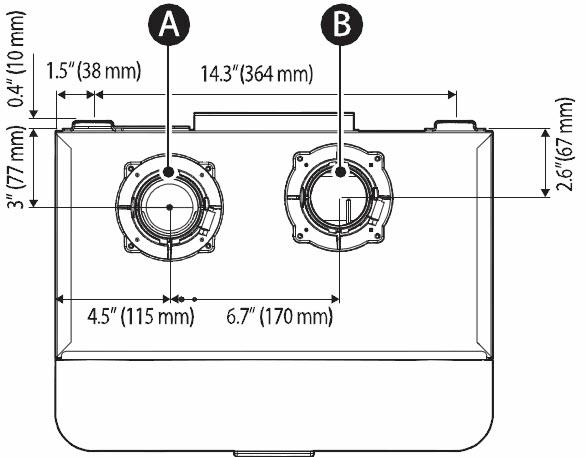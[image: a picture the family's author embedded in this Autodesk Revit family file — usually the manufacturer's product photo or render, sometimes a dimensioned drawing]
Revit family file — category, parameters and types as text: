
# Revit family: Water_Heater-Racks-Navien-NPE-12_Unit_Back_to_Back---
name_source: partatom
category: Mechanical Equipment
revit_build: Autodesk Revit 2016 (Build: 20150220_1215(x64)
units: mm (PartAtom-declared; Revit-internal decimal feet)

## family parameters
Cut with Voids When Loaded = No
Host = Face
OmniClass Number = 23.65.35.11
OmniClass Title = Supply Water Heaters
Part Type = Normal
Room Calculation Point = No
Round Connector Dimension = Use Diameter
Shared = No

## types (4) — shared parameters
2" Exhaust/Intake = Yes
3" Exhaust/Intake = No
Apparent Load = 0 VA
Assembly Code = D3010500
Certifications = Energy Star | AHRI | CSA | CSA | NFS
Cold Water Inlet = 1"
Configuration = NPE_B12_4B2B_4B2B
Default Elevation = 48 "
Depth = 23.8 "
Description = 12 Unit Back to Back
Exhaust = 2"
Finish = Metal - Navien - White
Flow Rate = 1 GPM
Flow Rate Note = 35°F (19°C) temp rise: 11.2 GPM (42 L/m) | 45°F (25°C) temp rise: 8.7 GPM (33 L/m) | 67°F (36°C) temp rise: NPE-240A: 5.6 GPM(21 L/m), NPE-240S: 5.7 GPM(22 L/m)
Frequency = 60 Hz
Gas Inlet = 1"
Heating Capacity = 120000.0 Btu/h
Heating Capacity Note = 19,900–199,900 (BTU/H)
Height = 65.5 "
Hot Water Outlet = 1"
Ignition = Electronic ignition
Installation Type = Indoor
Intake = 2"
Keynote = 22 33 00.A1
Manifold(s) = (2) 30019039A + (2) 30019042A
Manufacturer = Navien, Inc.
Manufacturer Fax Number = (949) 420-0430
Natural Gas Manifold Pressure = -0.05" WC to -0.58" WC
Natural Gas Supply Pressure = 3.5"–10.5" WC
Number of Poles = 1
Phase = 1
Power Factor = 1
Product Documentation Link = https://www.navieninc.com
Product Name = NPE Series Tankless Water Heaters w/ Racks
Product Page URL = https://www.navieninc.com
Propane Gas Manifold Pressure = -0.10" WC to -0.78" WC
Propane Gas Supply Pressure = 8"–13" WC
Rack(s) = (2) GFFM-KDIZUS-003 + (4) GFFM-KDIZUS-004
Required Cascade Operation Accessory = (12) 30014367A (Common Vent Damper & Cascade Communication Cable) or (11) GXXX000546 (Individual Vent Cascade Communication Cable)
URL = https://www.navieninc.com
Venting = Exhaust: 2" PVC, CPVC, PP, SS / 2" special gas vent type BH (Class II, A/B/C) | Intake: 2" PVC, CPVC, PP, SS / 2" special gas vent type BH (Class II, A/B/C) | Vent clearances: 0" to combustibles
Venting Type = Forced draft direct vent
Version = 2016 - v1.0.a
Voltage = 120 V
Water Pressure = 15–150 PSI
Wi-Fi Ready = NaviLink Wi-Fi Control: PBCM-AS-001
Width = 142.3 "

## per-type parameters (varying)
| type | Constraints | Model | Natural Gas | Propane Gas | Recirculation Inlet | Recirculation Inlet Visibility | Tankless Water Heaters | Weight |
| Natural Gas - Recirculating System - NPE-240A(Advanced)-NG | 6 | (12) NPE-240A-NG | Yes | No | 0" | Yes | (12) NPE-240A-NG | 82.00 lbf |
| Natural Gas - NPE-240S(Standard)-NG | 7 | (12) NPE-240S-NG | Yes | No | 1" | No | (12) NPE-240S-NG | 75.00 lbf |
| Propane Gas - Recirculating System - NPE-240A(Advanced)-LPG | 6 | (12) NPE-240A-LPG | No | Yes | 0" | Yes | (12) NPE-240A-LPG | 82.00 lbf |
| Propane Gas - NPE-240S(Standard)-LPG | 7 | (12) NPE-240S-LPG | No | Yes | 1" | No | (12) NPE-240S-LPG | 75.00 lbf |

## geometry (parser evidence)
native form markers: Sweep x21
no freeform markers — native parametric forms only
